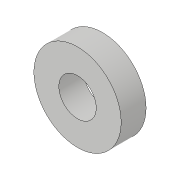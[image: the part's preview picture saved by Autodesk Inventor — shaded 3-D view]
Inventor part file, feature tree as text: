
AUTODESK INVENTOR PART (.ipt)
format: ipt  version: 2018.3 (Build 223284000, 284)  size: 81,920 bytes
history: native  units: in
note: dims shown in document units (in); Inventor stores cm internally (conversion verified against a paired STEP export)
features: extrude x1, sketch x1
ambient origin geometry x8: Origin, YZ Plane, XZ Plane, XY Plane, X Axis, Y Axis, Z Axis, Center Point
bodies: Solid1 (feature_tree)
feature tree (2):
  extrude  "Extrusion1"  Depth=0.25in
  sketch  "Sketch1"  dims[d0=0.375in d1=0.875in d2=0.25in d3=0.0in]
